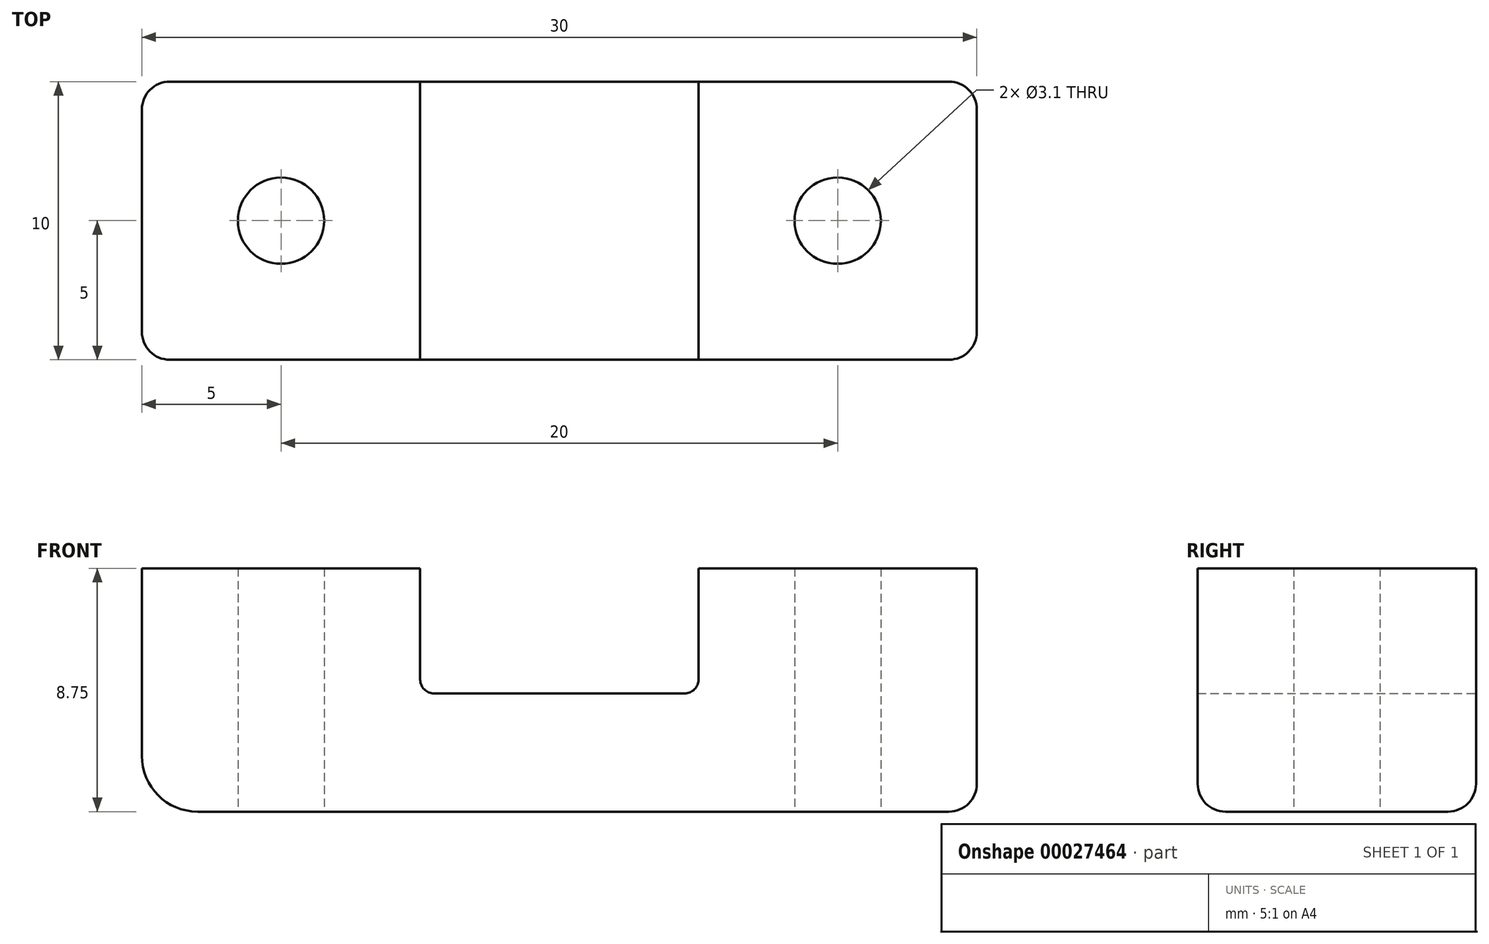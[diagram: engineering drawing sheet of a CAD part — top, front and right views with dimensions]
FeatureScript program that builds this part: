
annotation { "Feature Type Name" : "Feature", "Feature Type Description" : "" }
export const myFeature = defineFeature(function(context is Context, id is Id, definition is map)
    precondition{}
    {
        {
            var Q0;
            Q0=qCreatedBy(makeId("Front.planeOp"),FACE);
            var sketch = newSketch(context, id + "F0", { "sketchPlane" : qUnion([Q0])});
            skLineSegment(sketch, "E0", {"start": v(-15, 0) * mm, "end": v(-5, 0) * mm});
            skLineSegment(sketch, "E1", {"start": v(-5, 0) * mm, "end": v(-5, -4) * mm});
            skLineSegment(sketch, "E2", {"start": v(-4.5, -4.5) * mm, "end": v(4.5, -4.5) * mm});
            skLineSegment(sketch, "E3", {"start": v(5, -4) * mm, "end": v(5, 0) * mm});
            skLineSegment(sketch, "E4", {"start": v(5, 0) * mm, "end": v(15, 0) * mm});
            skLineSegment(sketch, "E5", {"start": v(15, 0) * mm, "end": v(15, -7.75) * mm});
            skLineSegment(sketch, "E6", {"start": v(14, -8.75) * mm, "end": v(-13, -8.75) * mm});
            skLineSegment(sketch, "E7", {"start": v(-15, -6.75) * mm, "end": v(-15, 0) * mm});
            skLineSegment(sketch, "E8", {"start": v(0, -4.5) * mm, "end": v(0, 0) * mm, "construction": true});
            skPoint(sketch, "E9.visualSharp", {"position": v(-5, -4.5) * mm});
            skArc(sketch, "E9.filletArc", {"start": v(-5, -4) * mm, "mid": v(-4.85, -4.35) * mm, "end": v(-4.5, -4.5) * mm});
            skPoint(sketch, "E10.visualSharp", {"position": v(5, -4.5) * mm});
            skArc(sketch, "E10.filletArc", {"start": v(4.5, -4.5) * mm, "mid": v(4.85, -4.35) * mm, "end": v(5, -4) * mm});
            skPoint(sketch, "E11.visualSharp", {"position": v(15, -8.75) * mm});
            skArc(sketch, "E11.filletArc", {"start": v(14, -8.75) * mm, "mid": v(14.7, -8.46) * mm, "end": v(15, -7.75) * mm});
            skPoint(sketch, "E12.visualSharp", {"position": v(-15, -8.75) * mm});
            skArc(sketch, "E12.filletArc", {"start": v(-15, -6.75) * mm, "mid": v(-14.41, -8.16) * mm, "end": v(-13, -8.75) * mm});
            skSolve(sketch);
        }
        {
            var Q0;
            Q0=makeQuery(id+"F0.imprint","IMPRINT",FACE,{"disambiguationData":[TD([[makeQuery(id+"F0.imprint","IMPRINT",EDGE,{"derivedFrom":sQuery(id+"F0.wireOp",EDGE,"E0")}),-1.0]])]});
            extrude(context, id + "F1", {"entities" : qUnion([Q0]), "depth" : 10 * mm, "symmetric" : true});
        }
        {
            var Q0;
            Q0=makeQuery(id+"F1.opExtrude","SWEPT_FACE",FACE,{"disambiguationData":[OSD([sQuery(id+"F0.wireOp",EDGE,"E6")])]});
            var sketch = newSketch(context, id + "F2", { "sketchPlane" : qUnion([Q0])});
            skCircle(sketch, "E13", {"center": v(-10, 0) * mm, "radius": 1.55 * mm});
            skCircle(sketch, "E14", {"center": v(10, 0) * mm, "radius": 1.55 * mm});
            skSolve(sketch);
        }
        {
            var Q0;
            Q0=makeQuery(id+"F2.imprint","IMPRINT",FACE,{"disambiguationData":[TD([[makeQuery(id+"F2.imprint","IMPRINT",EDGE,{"derivedFrom":sQuery(id+"F2.wireOp",EDGE,"E13")}),1.0]])]});
            var Q1;
            Q1=makeQuery(id+"F2.imprint","IMPRINT",FACE,{"disambiguationData":[TD([[makeQuery(id+"F2.imprint","IMPRINT",EDGE,{"derivedFrom":sQuery(id+"F2.wireOp",EDGE,"E14")}),1.0]])]});
            extrude(context, id + "F3", {"entities" : qUnion([Q0, Q1]), "operationType" : NewBodyOperationType.REMOVE, "endBound" : BoundingType.THROUGH_ALL, "oppositeDirection" : true, "depth" : 25 * mm});
        }
        {
            var Q0;
            Q0=makeQuery(id+"F1.opExtrude","CAP_EDGE",EDGE,{"disambiguationData":[OSD([sQuery(id+"F0.wireOp",EDGE,"E7")])],"isStart":false});
            var Q1;
            Q1=makeQuery(id+"F1.opExtrude","CAP_EDGE",EDGE,{"disambiguationData":[OSD([sQuery(id+"F0.wireOp",EDGE,"E7")])],"isStart":true});
            fillet(context, id + "F4", {"entities" : qUnion([Q0, Q1]), "radius" : 1 * mm, "tangentPropagation" : true, "allowEdgeOverflow" : false});
        }
    });
